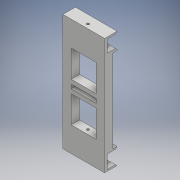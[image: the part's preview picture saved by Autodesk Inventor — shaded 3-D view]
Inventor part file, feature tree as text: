
AUTODESK INVENTOR PART (.ipt)
format: ipt  version: 2018 (Build 220112000, 112)  size: 419,840 bytes
history: native  units: mm
features: extrude x7, sketch x7, chamfer x3
ambient origin geometry x8: Origin, YZ Plane, XZ Plane, XY Plane, X Axis, Y Axis, Z Axis, Center Point
bodies: Solid1 (feature_tree)
feature tree (17):
  extrude  "Extrusion1"  Depth=140.0mm
  extrude  "Extrusion2"  Depth=10.0mm
  extrude  "Extrusion3"  Depth=5.0mm TaperAngle=0.0deg
  extrude  "Extrusion4"  Depth=10.0mm
  extrude  "Extrusion5"  Depth=10.0mm
  chamfer  "Chamfer1"  Distance=5.0mm
  chamfer  "Chamfer2"  Distance=50.0mm
  chamfer  "Chamfer3"  Distance=10.0mm
  extrude  "Extrusion8"  Depth=10.0mm
  extrude  "Extrusion9"  Depth=10.0mm
  sketch  "Sketch1"  dims[d0=50.0mm d1=140.0mm]
  sketch  "Sketch2"  dims[d2=10.0mm d3=0.0mm d4=20.0mm]
  sketch  "Sketch3"  dims[d5=20.0mm d6=5.0mm d7=0.0mm]
  sketch  "Sketch4"  dims[d8=5.0mm d9=10.0mm]
  sketch  "Sketch5"  dims[d10=5.0mm d11=10.0mm d12=5.0mm d13=0.0mm d15=50.0mm d16=0.0mm]
  sketch  "Sketch8"  dims[d17=10.0mm]
  sketch  "Sketch9"  dims[d18=10.0mm d19=10.0mm d21=10.0mm d22=2.5mm d23=5.0mm d24=5.0mm d25=5.0mm d26=10.0mm d27=0.0mm d28=7.0mm d29=2.0mm d30=45.0deg d31=5.0mm d32=2.0mm d33=45.0deg d34=3.0mm d35=2.0mm d36=45.0deg d46=2.0mm d53=5.0mm d54=3.0mm d55=30.0mm d56=0.0mm d57=5.0mm d58=30.0mm d59=0.0mm d60=2.0mm]
